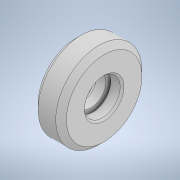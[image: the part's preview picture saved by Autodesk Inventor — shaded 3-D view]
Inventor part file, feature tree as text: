
AUTODESK INVENTOR PART (.ipt)
format: ipt  version: 2022 (Build 260153000, 153)  size: 164,352 bytes
history: native  units: mm
features: sketch x3, revolve x2, other x1, hole x1
ambient origin geometry x8: Origin, YZ Plane, XZ Plane, XY Plane, X Axis, Y Axis, Z Axis, Center Point
bodies: Body1 (feature_tree)
feature tree (7):
  other  "Твердое тело1"
  revolve  "Вращение1"
  hole  "Отверстие1"  [1 undecoded]
  revolve  "Вращение2"
  sketch  "Эскиз1"
  sketch  "Эскиз2"
  sketch  "Эскиз3"
note: 1 required parameter value undecoded (feature->parameter linkage not recoverable at this tier; creation-order binding heuristic only, values carry confidence <= 0.55)
